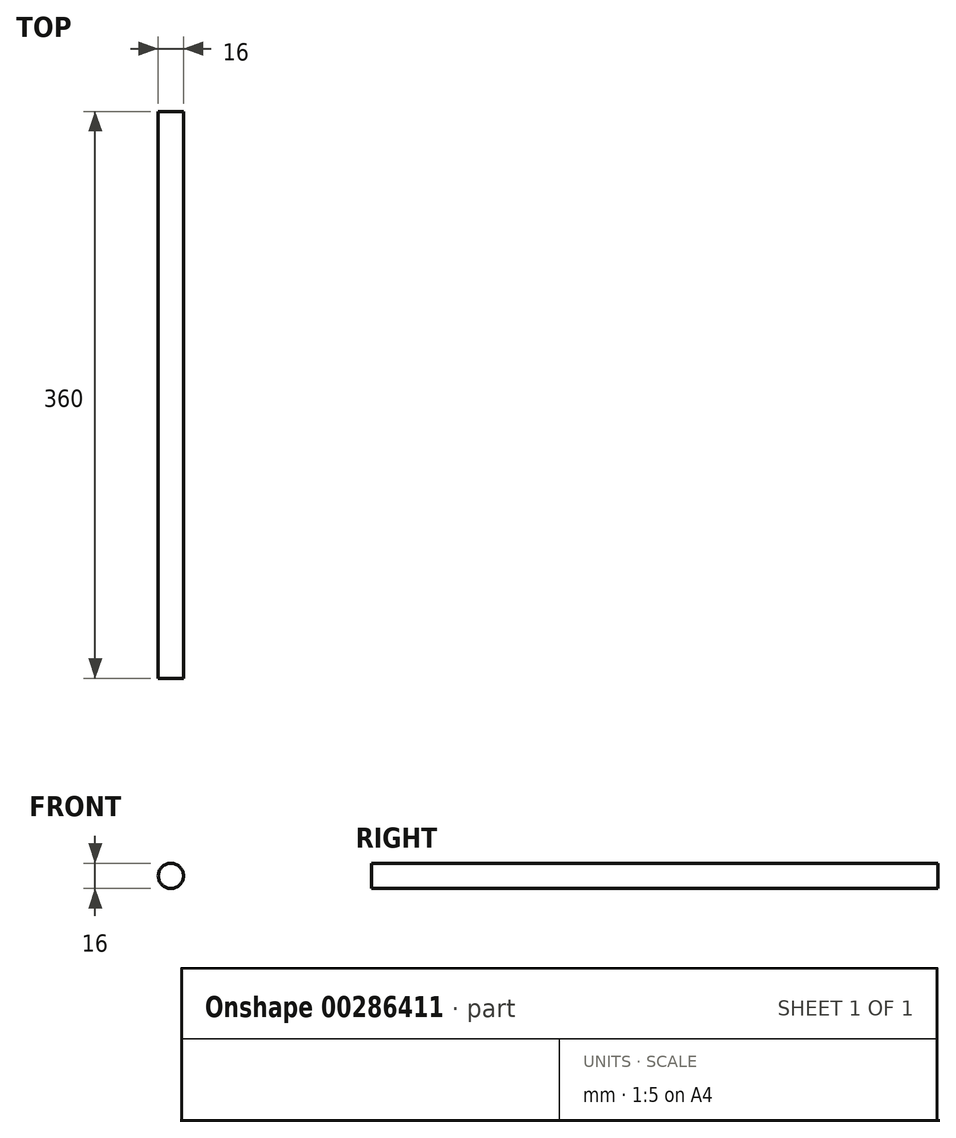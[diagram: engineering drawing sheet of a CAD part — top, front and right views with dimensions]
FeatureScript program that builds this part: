
annotation { "Feature Type Name" : "Feature", "Feature Type Description" : "" }
export const myFeature = defineFeature(function(context is Context, id is Id, definition is map)
    precondition{}
    {
        {
            var Q0;
            Q0=qCreatedBy(makeId("Front.planeOp"),FACE);
            var sketch = newSketch(context, id + "F0", { "sketchPlane" : qUnion([Q0])});
            skCircle(sketch, "E0", {"center": v(0, 0) * mm, "radius": 8 * mm});
            skSolve(sketch);
        }
        {
            var Q0;
            Q0 = qSketchRegion(id + "F0", true);
            extrude(context, id + "F1", {"entities" : qUnion([Q0]), "depth" : 360 * mm});
        }
    });
